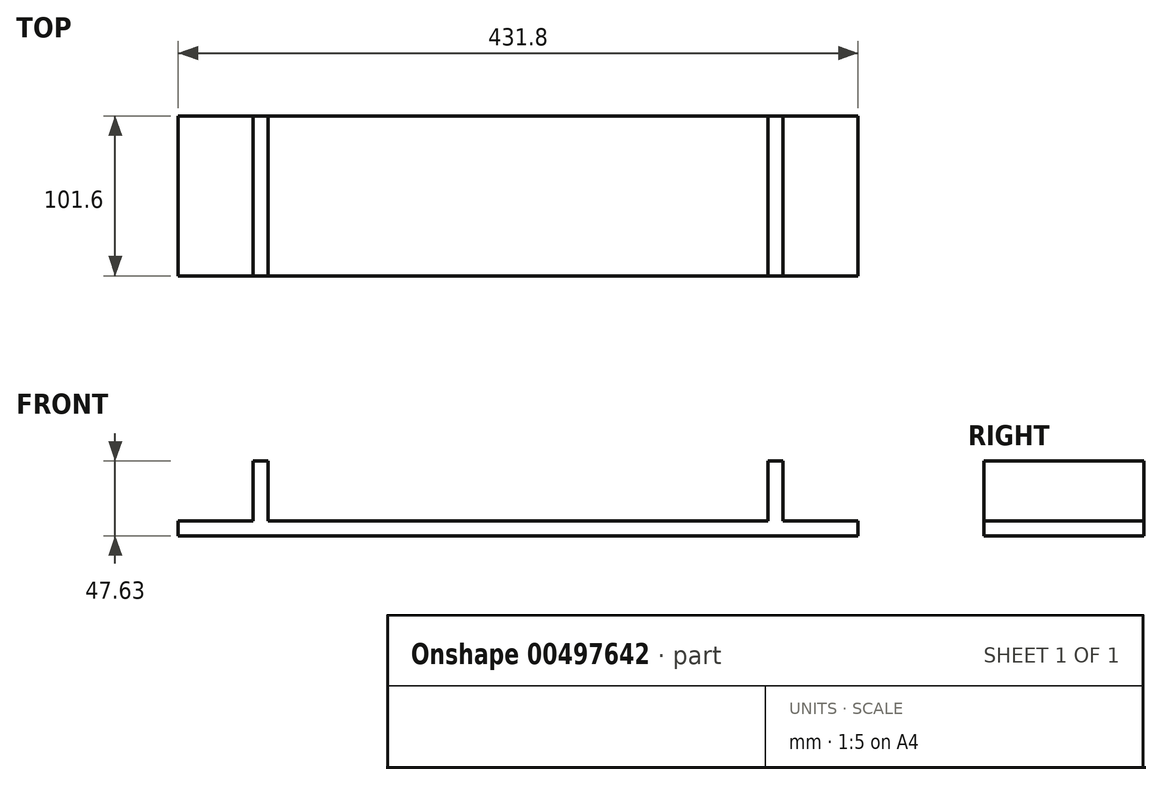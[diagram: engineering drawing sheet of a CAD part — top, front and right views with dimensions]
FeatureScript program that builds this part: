
annotation { "Feature Type Name" : "Feature", "Feature Type Description" : "" }
export const myFeature = defineFeature(function(context is Context, id is Id, definition is map)
    precondition{}
    {
        {
            var Q0;
            Q0=qCreatedBy(makeId("Top.planeOp"),FACE);
            var sketch = newSketch(context, id + "F0", { "sketchPlane" : qUnion([Q0])});
            skLineSegment(sketch, "E0.bottom", {"start": v(215.9, -50.8) * mm, "end": v(-215.9, -50.8) * mm});
            skLineSegment(sketch, "E0.top", {"start": v(215.9, 50.8) * mm, "end": v(-215.9, 50.8) * mm});
            skLineSegment(sketch, "E0.left", {"start": v(215.9, -50.8) * mm, "end": v(215.9, 50.8) * mm});
            skLineSegment(sketch, "E0.right", {"start": v(-215.9, -50.8) * mm, "end": v(-215.9, 50.8) * mm});
            skPoint(sketch, "E0.middle", {"position": v(0, 0) * mm});
            skSolve(sketch);
        }
        {
            var Q0;
            Q0 = qSketchRegion(id + "F0", true);
            extrude(context, id + "F1", {"entities" : qUnion([Q0]), "oppositeDirection" : true, "depth" : 9.52 * mm});
        }
        {
            var Q0;
            Q0=qCreatedBy(makeId("Front.planeOp"),FACE);
            var sketch = newSketch(context, id + "F2", { "sketchPlane" : qUnion([Q0])});
            skLineSegment(sketch, "E1.bottom", {"start": v(-168.28, 38.1) * mm, "end": v(-158.75, 38.1) * mm});
            skLineSegment(sketch, "E1.top", {"start": v(-168.28, 0) * mm, "end": v(-158.75, 0) * mm});
            skLineSegment(sketch, "E1.left", {"start": v(-168.28, 38.1) * mm, "end": v(-168.28, 0) * mm});
            skLineSegment(sketch, "E1.right", {"start": v(-158.75, 38.1) * mm, "end": v(-158.75, 0) * mm});
            skLineSegment(sketch, "E2.MirrorCS", {"start": v(158.75, 38.1) * mm, "end": v(158.75, 0) * mm});
            skLineSegment(sketch, "E3.MirrorCS", {"start": v(168.28, 38.1) * mm, "end": v(168.28, 0) * mm});
            skLineSegment(sketch, "E4.MirrorCS", {"start": v(168.28, 38.1) * mm, "end": v(158.75, 38.1) * mm});
            skSolve(sketch);
        }
        {
            var Q0;
            Q0=makeQuery(id+"F2.imprint","IMPRINT",FACE,{"disambiguationData":[TD([[makeQuery(id+"F2.imprint","IMPRINT",EDGE,{"derivedFrom":sQuery(id+"F2.wireOp",EDGE,"E1.bottom")}),-1.0]])]});
            extrude(context, id + "F3", {"entities" : qUnion([Q0]), "operationType" : NewBodyOperationType.ADD, "endBound" : BoundingType.SYMMETRIC, "depth" : 101.6 * mm});
        }
        {
            var Q0;
            Q0=qCreatedBy(makeId("Front.planeOp"),FACE);
            var sketch = newSketch(context, id + "F4", { "sketchPlane" : qUnion([Q0])});
            skLineSegment(sketch, "E5.bottom", {"start": v(158.75, 38.1) * mm, "end": v(168.28, 38.1) * mm});
            skLineSegment(sketch, "E5.top", {"start": v(158.75, 0) * mm, "end": v(168.28, 0) * mm});
            skLineSegment(sketch, "E5.left", {"start": v(158.75, 38.1) * mm, "end": v(158.75, 0) * mm});
            skLineSegment(sketch, "E5.right", {"start": v(168.28, 38.1) * mm, "end": v(168.28, 0) * mm});
            skSolve(sketch);
        }
        {
            var Q0;
            Q0 = qSketchRegion(id + "F4", true);
            extrude(context, id + "F5", {"entities" : qUnion([Q0]), "operationType" : NewBodyOperationType.ADD, "endBound" : BoundingType.SYMMETRIC, "depth" : 101.6 * mm});
        }
    });
